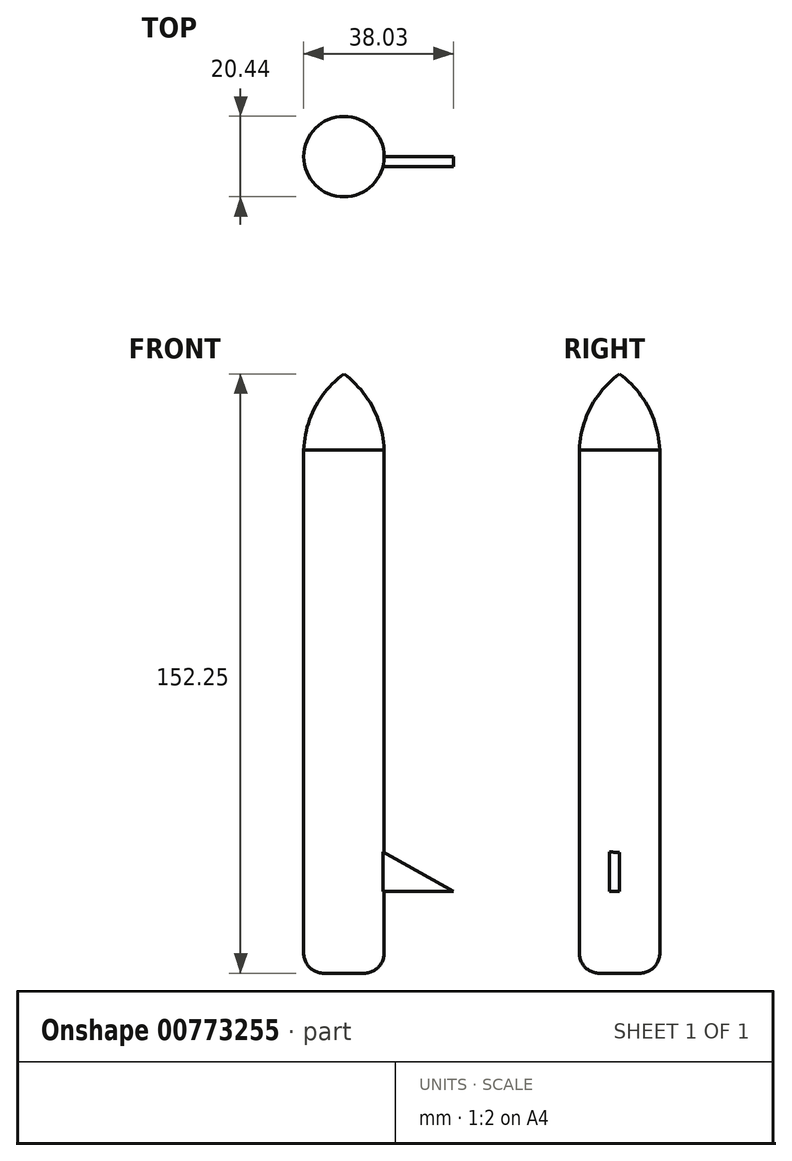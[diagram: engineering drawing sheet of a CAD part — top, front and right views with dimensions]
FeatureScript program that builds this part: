
annotation { "Feature Type Name" : "Feature", "Feature Type Description" : "" }
export const myFeature = defineFeature(function(context is Context, id is Id, definition is map)
    precondition{}
    {
        {
            var Q0;
            Q0=qCreatedBy(makeId("Front.planeOp"),FACE);
            var sketch = newSketch(context, id + "F0", { "sketchPlane" : qUnion([Q0])});
            skLineSegment(sketch, "E0", {"start": v(0, 75.84) * mm, "end": v(0, -76.41) * mm});
            skArc(sketch, "E1", {"start": v(10.22, 56.55) * mm, "mid": v(7.31, 67.36) * mm, "end": v(0, 75.84) * mm});
            skLineSegment(sketch, "E2", {"start": v(10.22, 56.55) * mm, "end": v(10.22, -76.41) * mm});
            skLineSegment(sketch, "E3", {"start": v(10.22, -76.41) * mm, "end": v(0, -76.41) * mm});
            skSolve(sketch);
        }
        {
            var Q0;
            Q0 = qSketchRegion(id + "F0", true);
            var Q1;
            Q1=sQuery(id+"F0.wireOp",EDGE,"E0");
            revolve(context, id + "F1", {"surfaceOperationType" : NewSurfaceOperationType.NEW, "entities" : qUnion([Q0]), "axis" : qUnion([Q1]), "revolveType" : RevolveType.FULL});
        }
        {
            var Q0;
            Q0=makeQuery(id+"F1.opRevolve","SWEPT_FACE",FACE,{"disambiguationData":[OSD([sQuery(id+"F0.wireOp",EDGE,"E3")])]});
            fillet(context, id + "F2", {"entities" : qUnion([Q0]), "radius" : 5.08 * mm, "tangentPropagation" : true, "allowEdgeOverflow" : false});
        }
        {
            var Q0;
            Q0=qCreatedBy(makeId("Front.planeOp"),FACE);
            var sketch = newSketch(context, id + "F3", { "sketchPlane" : qUnion([Q0])});
            skLineSegment(sketch, "E4", {"start": v(0, -40.02) * mm, "end": v(0, -55.59) * mm});
            skLineSegment(sketch, "E5", {"start": v(0, -55.59) * mm, "end": v(27.81, -55.59) * mm});
            skLineSegment(sketch, "E6", {"start": v(27.81, -55.59) * mm, "end": v(0, -40.02) * mm});
            skSolve(sketch);
        }
        {
            var Q0;
            Q0 = qSketchRegion(id + "F3", true);
            extrude(context, id + "F4", {"entities" : qUnion([Q0]), "operationType" : NewBodyOperationType.ADD, "depth" : 2.54 * mm, "offsetDistance" : 25.4 * mm});
        }
    });
